# Revit family: Kitchen_Appliances_Electrolux-Brasil_Stainless-Steel-Dishwasher-10-Places-Set
name_source: partatom
category: Specialty Equipment
revit_build: Autodesk Revit 2016 (Build: 20151007_0715(x64)
units: mm (PartAtom-declared; Revit-internal decimal feet)

## family parameters
Always vertical = No
Cut with Voids When Loaded = No
OmniClass Number = 23.21.23.25
Part Type = Normal
Room Calculation Point = No
Round Connector Dimension = Use Diameter
Shared = No
Work Plane-Based = No

## types (1)
- Stainless Steel Dishwasher 10 Places Settings
    BIMobject category = Appliances
    BIMobject category code = kitchen-appliances
    BIMobject main category = Kitchen
    BIMobject main category code = kitchen
    Design country = Brazil
    Edition number = 1
    IFC Classification = Electric Appliance
    Installation instructions = https://www.youtube.com
    Manufacturer country = Brazil
    Manufacturer name = Electrolux Brasil
    Masterformat 2014 Code = 11 48 13
    Masterformat 2014 Description = Commercial Dishwashers
    Material main = Steel
    NBS Reference Code = 31-23
    NBS Reference Description = Dishwashers
    OmniClass Code = 23-21 23 25
    OmniClass Description = Residential Dishwashers
    Product Guid = 46e1fa87-7722-49e3-9b8f-845da3914e14
    Product SKU = LV10X
    Product certification = https://www.electrolux-ui.com
    Product data url = https://bimobject.com
    Product family = Appliances
    Product group = Dishwashers
    Product name = Stainless Steel Dishwasher 10 Places Settings
    Product url = https://loja.electrolux.com.br
    QR code = http://bimobject.com
    Technical description = https://www.electrolux-ui.com
    Uniclass 1.4 Code = L7231
    Uniclass 1.4 Description = Dishwashers
    Uniclass 2.0 Code = PR-31-23
    Uniclass 2.0 Description = Dishwashers
    Uniclass 2015 Code = Pr_40_70_21
    Uniclass 2015 Name = Dishwashers
    Youtube clip = https://www.youtube.com

## geometry (parser evidence)
native form markers: Sweep x4
no freeform markers — native parametric forms only
